# Revit family: QSP2
name_source: partatom
category: Lighting Fixtures
units: mm (PartAtom-declared; Revit-internal decimal feet)

## family parameters
Cut with Voids When Loaded = No
Host = Face
Light Source = Yes
OmniClass Number = 23.80.70.11
OmniClass Title = Luminaries for Internal Lighting
Part Type = Normal
Room Calculation Point = No
Round Connector Dimension = Use Diameter
Shared = No

## types (1)
- QSP2
    Apparent Load = 0 VA
    Color Filter = 16777215
    Default Elevation = 48"
    Description = Architectural wallpack in two stylish shapes.
    Dimming Lamp Color Temperature Shift = <None>
    Finish = Paint - Textured Camera Black
    Lamp = LED
    Load Classification = Lighting
    Manufacturer = EXO
    Model = QSP2
    Opal lens = Glass - White
    Photometric Web File = TRP2-24L-30-3K7-1 (2).ies
    Tilt Angle = -120.00°
    URL = https://www.currentlighting.com
    Voltage = 120 V
    Wattage Comments = 30W

## geometry (parser evidence)
native form markers: Sweep x1
no freeform markers — native parametric forms only
